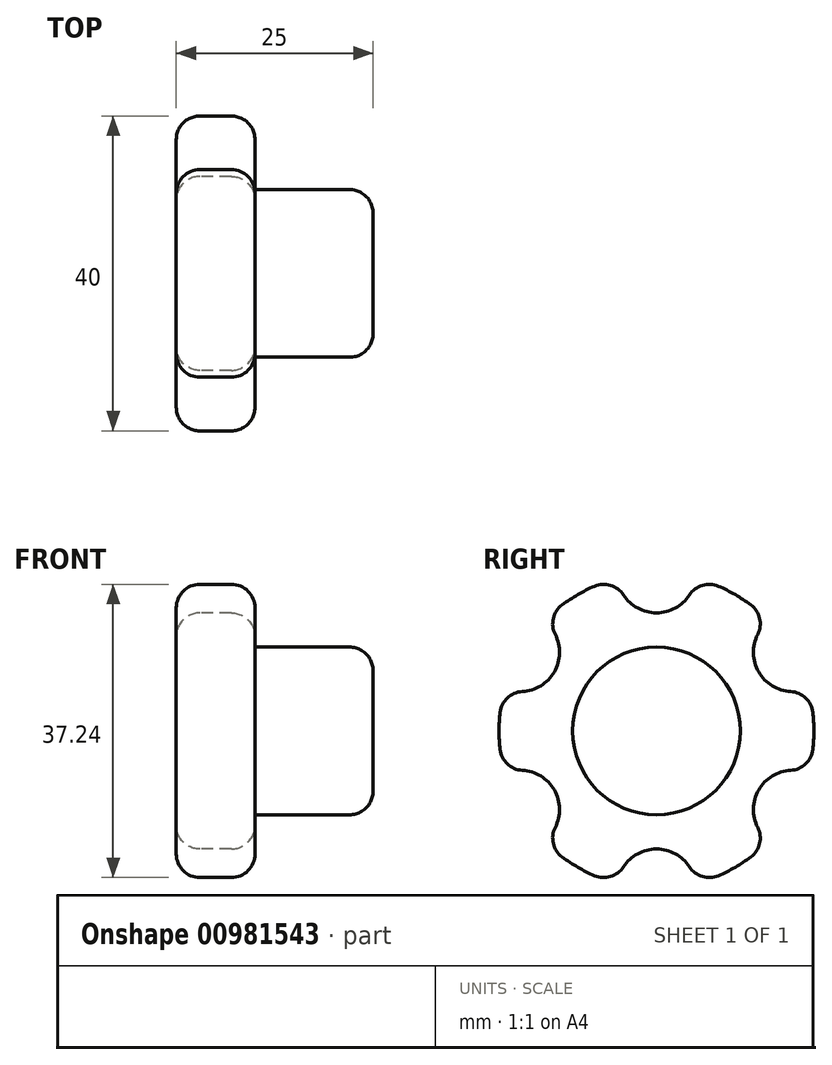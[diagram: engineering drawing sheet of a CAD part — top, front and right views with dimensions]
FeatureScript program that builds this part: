
annotation { "Feature Type Name" : "Feature", "Feature Type Description" : "" }
export const myFeature = defineFeature(function(context is Context, id is Id, definition is map)
    precondition{}
    {
        {
            var Q0;
            Q0=qCreatedBy(makeId("Right.planeOp"),FACE);
            var sketch = newSketch(context, id + "F0", { "sketchPlane" : qUnion([Q0])});
            skCircle(sketch, "E0", {"center": v(0, 0) * mm, "radius": 20 * mm});
            skSolve(sketch);
        }
        {
            var Q0;
            Q0 = qSketchRegion(id + "F0", true);
            extrude(context, id + "F1", {"entities" : qUnion([Q0]), "depth" : 10 * mm, "offsetDistance" : 25 * mm});
        }
        {
            var Q0;
            Q0=makeQuery(id+"F1.opExtrude","CAP_FACE",FACE,{"disambiguationData":[OSD([sQuery(id+"F0.wireOp",EDGE,"E0")])],"isStart":false});
            var sketch = newSketch(context, id + "F2", { "sketchPlane" : qUnion([Q0])});
            skCircle(sketch, "E1", {"center": v(0, 0) * mm, "radius": 10.65 * mm});
            skSolve(sketch);
        }
        {
            var Q0;
            Q0 = qSketchRegion(id + "F2", true);
            extrude(context, id + "F3", {"entities" : qUnion([Q0]), "operationType" : NewBodyOperationType.ADD, "depth" : 15 * mm, "offsetDistance" : 25 * mm});
        }
        {
            var Q0;
            Q0=qCreatedBy(makeId("Right.planeOp"),FACE);
            var sketch = newSketch(context, id + "F4", { "sketchPlane" : qUnion([Q0])});
            skCircle(sketch, "E2", {"center": v(0, 20) * mm, "radius": 5 * mm});
            skCircle(sketch, "E3.1.0", {"center": v(-17.32, 10) * mm, "radius": 5 * mm});
            skCircle(sketch, "E3.2.0", {"center": v(-17.32, -10) * mm, "radius": 5 * mm});
            skCircle(sketch, "E3.3.0", {"center": v(0, -20) * mm, "radius": 5 * mm});
            skCircle(sketch, "E3.4.0", {"center": v(17.32, -10) * mm, "radius": 5 * mm});
            skCircle(sketch, "E3.5.0", {"center": v(17.32, 10) * mm, "radius": 5 * mm});
            skPoint(sketch, "E3.center", {"position": v(0, 0) * mm});
            skSolve(sketch);
        }
        {
            var Q0;
            Q0 = qSketchRegion(id + "F4", true);
            extrude(context, id + "F5", {"entities" : qUnion([Q0]), "operationType" : NewBodyOperationType.REMOVE, "depth" : 25 * mm, "offsetDistance" : 25 * mm});
        }
        {
            var Q0;
            Q0=makeQuery(id+"F5.boolean.opBoolean","INTERSECT",EDGE,{"disambiguationData":[OD(0.0)],"derivedFrom":[makeQuery(id+"F1.opExtrude","SWEPT_FACE",FACE,{"disambiguationData":[OSD([sQuery(id+"F0.wireOp",EDGE,"E0")])]}),makeQuery(id+"F5.opExtrude","SWEPT_FACE",FACE,{"disambiguationData":[OSD([sQuery(id+"F4.wireOp",EDGE,"E3.5.0")])]})]});
            var Q1;
            Q1=makeQuery(id+"F5.boolean.opBoolean","INTERSECT",EDGE,{"disambiguationData":[OD(1.0)],"derivedFrom":[makeQuery(id+"F1.opExtrude","SWEPT_FACE",FACE,{"disambiguationData":[OSD([sQuery(id+"F0.wireOp",EDGE,"E0")])]}),makeQuery(id+"F5.opExtrude","SWEPT_FACE",FACE,{"disambiguationData":[OSD([sQuery(id+"F4.wireOp",EDGE,"E2")])]})]});
            var Q2;
            Q2=makeQuery(id+"F5.boolean.opBoolean","INTERSECT",EDGE,{"disambiguationData":[OD(0.0)],"derivedFrom":[makeQuery(id+"F1.opExtrude","SWEPT_FACE",FACE,{"disambiguationData":[OSD([sQuery(id+"F0.wireOp",EDGE,"E0")])]}),makeQuery(id+"F5.opExtrude","SWEPT_FACE",FACE,{"disambiguationData":[OSD([sQuery(id+"F4.wireOp",EDGE,"E2")])]})]});
            var Q3;
            Q3=makeQuery(id+"F5.boolean.opBoolean","INTERSECT",EDGE,{"disambiguationData":[OD(0.0)],"derivedFrom":[makeQuery(id+"F1.opExtrude","SWEPT_FACE",FACE,{"disambiguationData":[OSD([sQuery(id+"F0.wireOp",EDGE,"E0")])]}),makeQuery(id+"F5.opExtrude","SWEPT_FACE",FACE,{"disambiguationData":[OSD([sQuery(id+"F4.wireOp",EDGE,"E3.1.0")])]})]});
            var Q4;
            Q4=makeQuery(id+"F5.boolean.opBoolean","INTERSECT",EDGE,{"disambiguationData":[OD(1.0)],"derivedFrom":[makeQuery(id+"F1.opExtrude","SWEPT_FACE",FACE,{"disambiguationData":[OSD([sQuery(id+"F0.wireOp",EDGE,"E0")])]}),makeQuery(id+"F5.opExtrude","SWEPT_FACE",FACE,{"disambiguationData":[OSD([sQuery(id+"F4.wireOp",EDGE,"E3.1.0")])]})]});
            var Q5;
            Q5=makeQuery(id+"F5.boolean.opBoolean","INTERSECT",EDGE,{"disambiguationData":[OD(1.0)],"derivedFrom":[makeQuery(id+"F1.opExtrude","SWEPT_FACE",FACE,{"disambiguationData":[OSD([sQuery(id+"F0.wireOp",EDGE,"E0")])]}),makeQuery(id+"F5.opExtrude","SWEPT_FACE",FACE,{"disambiguationData":[OSD([sQuery(id+"F4.wireOp",EDGE,"E3.5.0")])]})]});
            var Q6;
            Q6=makeQuery(id+"F5.boolean.opBoolean","INTERSECT",EDGE,{"disambiguationData":[OD(0.0)],"derivedFrom":[makeQuery(id+"F1.opExtrude","SWEPT_FACE",FACE,{"disambiguationData":[OSD([sQuery(id+"F0.wireOp",EDGE,"E0")])]}),makeQuery(id+"F5.opExtrude","SWEPT_FACE",FACE,{"disambiguationData":[OSD([sQuery(id+"F4.wireOp",EDGE,"E3.2.0")])]})]});
            var Q7;
            Q7=makeQuery(id+"F5.boolean.opBoolean","INTERSECT",EDGE,{"disambiguationData":[OD(1.0)],"derivedFrom":[makeQuery(id+"F1.opExtrude","SWEPT_FACE",FACE,{"disambiguationData":[OSD([sQuery(id+"F0.wireOp",EDGE,"E0")])]}),makeQuery(id+"F5.opExtrude","SWEPT_FACE",FACE,{"disambiguationData":[OSD([sQuery(id+"F4.wireOp",EDGE,"E3.2.0")])]})]});
            var Q8;
            Q8=makeQuery(id+"F5.boolean.opBoolean","INTERSECT",EDGE,{"disambiguationData":[OD(0.0)],"derivedFrom":[makeQuery(id+"F1.opExtrude","SWEPT_FACE",FACE,{"disambiguationData":[OSD([sQuery(id+"F0.wireOp",EDGE,"E0")])]}),makeQuery(id+"F5.opExtrude","SWEPT_FACE",FACE,{"disambiguationData":[OSD([sQuery(id+"F4.wireOp",EDGE,"E3.3.0")])]})]});
            var Q9;
            Q9=makeQuery(id+"F5.boolean.opBoolean","INTERSECT",EDGE,{"disambiguationData":[OD(1.0)],"derivedFrom":[makeQuery(id+"F1.opExtrude","SWEPT_FACE",FACE,{"disambiguationData":[OSD([sQuery(id+"F0.wireOp",EDGE,"E0")])]}),makeQuery(id+"F5.opExtrude","SWEPT_FACE",FACE,{"disambiguationData":[OSD([sQuery(id+"F4.wireOp",EDGE,"E3.3.0")])]})]});
            var Q10;
            Q10=makeQuery(id+"F5.boolean.opBoolean","INTERSECT",EDGE,{"disambiguationData":[OD(0.0)],"derivedFrom":[makeQuery(id+"F1.opExtrude","SWEPT_FACE",FACE,{"disambiguationData":[OSD([sQuery(id+"F0.wireOp",EDGE,"E0")])]}),makeQuery(id+"F5.opExtrude","SWEPT_FACE",FACE,{"disambiguationData":[OSD([sQuery(id+"F4.wireOp",EDGE,"E3.4.0")])]})]});
            var Q11;
            Q11=makeQuery(id+"F5.boolean.opBoolean","INTERSECT",EDGE,{"disambiguationData":[OD(1.0)],"derivedFrom":[makeQuery(id+"F1.opExtrude","SWEPT_FACE",FACE,{"disambiguationData":[OSD([sQuery(id+"F0.wireOp",EDGE,"E0")])]}),makeQuery(id+"F5.opExtrude","SWEPT_FACE",FACE,{"disambiguationData":[OSD([sQuery(id+"F4.wireOp",EDGE,"E3.4.0")])]})]});
            fillet(context, id + "F6", {"entities" : qUnion([Q0, Q1, Q2, Q3, Q4, Q5, Q6, Q7, Q8, Q9, Q10, Q11]), "radius" : 3 * mm, "tangentPropagation" : true, "allowEdgeOverflow" : false});
        }
        {
            var Q0;
            {var subQ0=sQuery(id+"F0.wireOp",EDGE,"E0");Q0=makeQuery(id+"F6.opFillet","BLEND_EDGE",EDGE,{"blendedFrom":[makeQuery(id+"F5.boolean.opBoolean","INTERSECT",EDGE,{"disambiguationData":[OD(1.0)],"derivedFrom":[makeQuery(id+"F1.opExtrude","SWEPT_FACE",FACE,{"disambiguationData":[OSD([subQ0])]}),makeQuery(id+"F5.opExtrude","SWEPT_FACE",FACE,{"disambiguationData":[OSD([sQuery(id+"F4.wireOp",EDGE,"E3.4.0")])]})]}),makeQuery(id+"F1.opExtrude","CAP_FACE",FACE,{"disambiguationData":[OSD([subQ0])],"isStart":false})],"blendedInto":[makeQuery(id+"F1.opExtrude","CAP_FACE",FACE,{"disambiguationData":[OSD([subQ0])],"isStart":false})]});}
            var Q1;
            {var subQ0=sQuery(id+"F0.wireOp",EDGE,"E0");Q1=makeQuery(id+"F6.opFillet","BLEND_EDGE",EDGE,{"blendedFrom":[makeQuery(id+"F5.boolean.opBoolean","INTERSECT",EDGE,{"disambiguationData":[OD(1.0)],"derivedFrom":[makeQuery(id+"F1.opExtrude","SWEPT_FACE",FACE,{"disambiguationData":[OSD([subQ0])]}),makeQuery(id+"F5.opExtrude","SWEPT_FACE",FACE,{"disambiguationData":[OSD([sQuery(id+"F4.wireOp",EDGE,"E3.4.0")])]})]}),makeQuery(id+"F1.opExtrude","CAP_FACE",FACE,{"disambiguationData":[OSD([subQ0])],"isStart":true})],"blendedInto":[makeQuery(id+"F1.opExtrude","CAP_FACE",FACE,{"disambiguationData":[OSD([subQ0])],"isStart":true})]});}
            fillet(context, id + "F7", {"entities" : qUnion([Q0, Q1]), "radius" : 3 * mm, "tangentPropagation" : true, "allowEdgeOverflow" : false});
        }
        {
            var Q0;
            Q0=makeQuery(id+"F3.opExtrude","CAP_EDGE",EDGE,{"disambiguationData":[OSD([sQuery(id+"F2.wireOp",EDGE,"E1")])],"isStart":false});
            fillet(context, id + "F8", {"entities" : qUnion([Q0]), "radius" : 3 * mm, "tangentPropagation" : true, "allowEdgeOverflow" : false});
        }
    });
